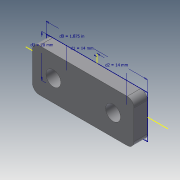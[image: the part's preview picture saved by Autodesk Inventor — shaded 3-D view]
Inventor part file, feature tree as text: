
AUTODESK INVENTOR PART (.ipt)
format: ipt  version: 2020.3 (Build 243373000, 373)  size: 112,128 bytes
history: native  units: in
note: dims shown in document units (in); Inventor stores cm internally (conversion verified against a paired STEP export)
features: sketch x1, extrude x1, hole x1, fillet x1
ambient origin geometry x8: Origin, YZ Plane, XZ Plane, XY Plane, X Axis, Y Axis, Z Axis, Center Point
bodies: Solid1 (feature_tree)
feature tree (4):
  sketch  "Sketch1"  dims[d0=1.875in d1=0.5512in d2=0.5512in d3=0.7874in d4=0.25in d5=0.0in d6=0.275in d7=0.75in d8=0.375in d9=0.25in d10=0.5635in d11=1.0in d12=0.8108in d13=0.125in]
  extrude  "Extrusion1"  Depth=0.125in
  hole  "Hole1"  [1 undecoded]
  fillet  "Fillet1"  Radius=0.7874in
note: 1 required parameter value undecoded (feature->parameter linkage not recoverable at this tier; creation-order binding heuristic only, values carry confidence <= 0.55)
